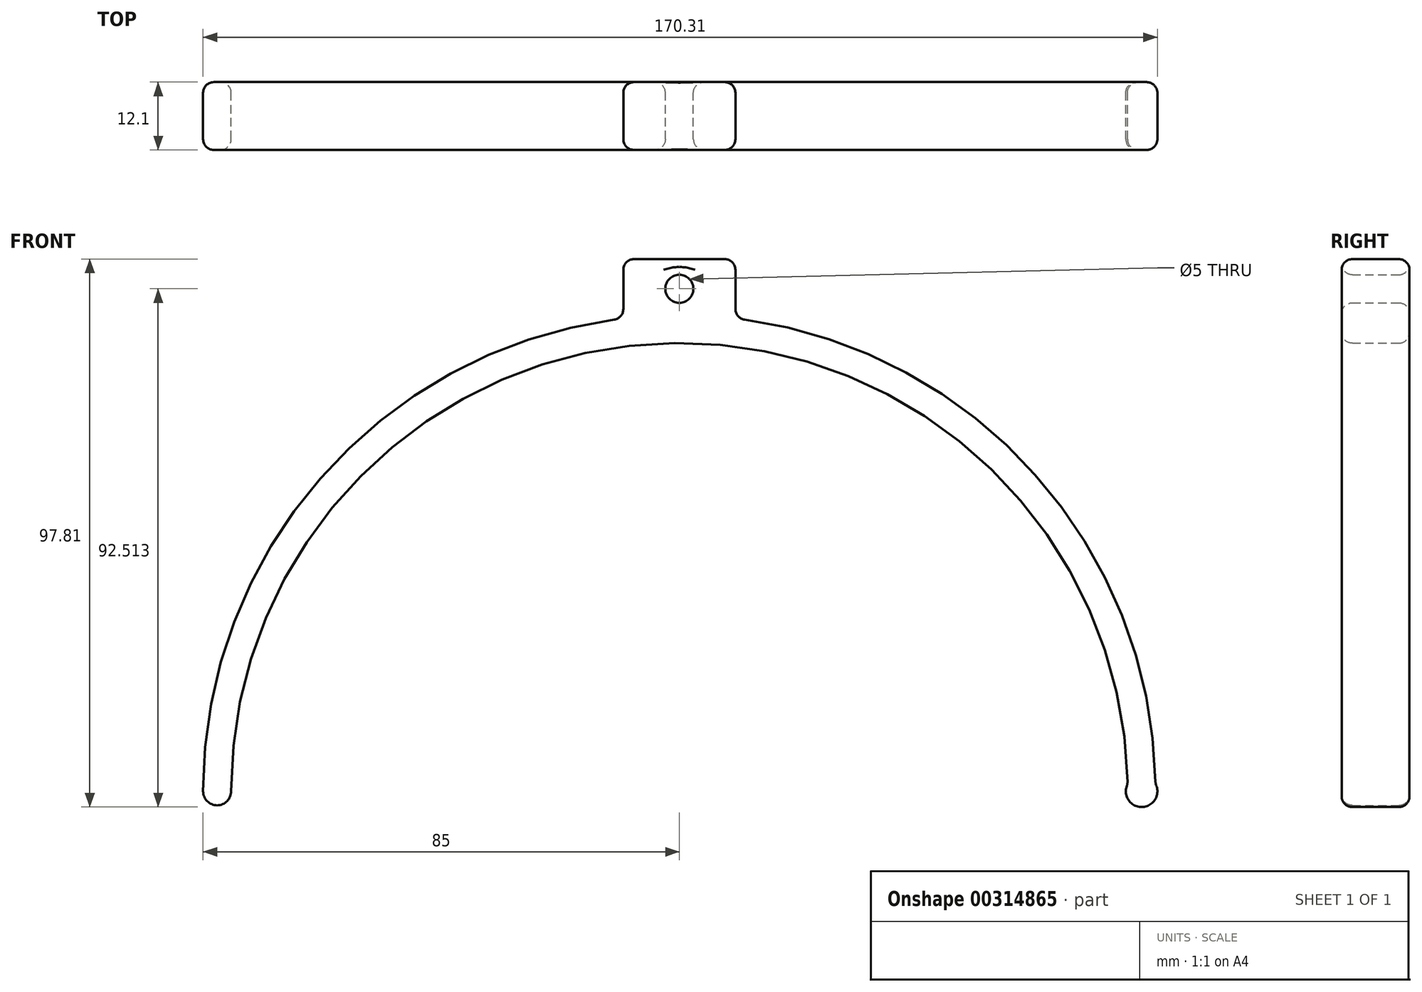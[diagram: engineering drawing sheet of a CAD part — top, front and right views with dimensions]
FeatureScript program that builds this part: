
annotation { "Feature Type Name" : "Feature", "Feature Type Description" : "" }
export const myFeature = defineFeature(function(context is Context, id is Id, definition is map)
    precondition{}
    {
        {
            var Q0;
            Q0=qCreatedBy(makeId("Front.planeOp"),FACE);
            var sketch = newSketch(context, id + "F0", { "sketchPlane" : qUnion([Q0])});
            skArc(sketch, "E0", {"start": v(79.99, -1.27) * mm, "mid": v(0.63, 80) * mm, "end": v(-80, 0) * mm});
            skArc(sketch, "E1", {"start": v(84.99, -1.3) * mm, "mid": v(63.97, 55.97) * mm, "end": v(10, 84.4) * mm});
            skLineSegment(sketch, "E2", {"start": v(0, 0) * mm, "end": v(0, 85) * mm, "construction": true});
            skLineSegment(sketch, "E3", {"start": v(0, 95) * mm, "end": v(10, 95) * mm, "construction": true});
            skLineSegment(sketch, "E4", {"start": v(0, 95) * mm, "end": v(-10, 95) * mm, "construction": true});
            skLineSegment(sketch, "E5", {"start": v(-10, 95) * mm, "end": v(-10, 84.4) * mm});
            skLineSegment(sketch, "E6", {"start": v(10, 95) * mm, "end": v(10, 84.4) * mm});
            skLineSegment(sketch, "E7", {"start": v(80, 0) * mm, "end": v(85, 0) * mm, "construction": true});
            skLineSegment(sketch, "E8", {"start": v(-80, 0) * mm, "end": v(-82.5, 0) * mm, "construction": true});
            skArc(sketch, "E9", {"start": v(-85, 0) * mm, "mid": v(-82.5, -2.5) * mm, "end": v(-80, 0) * mm});
            skArc(sketch, "E10", {"start": v(79.99, 1.27) * mm, "mid": v(82.52, -2.81) * mm, "end": v(84.99, 1.3) * mm});
            skLineSegment(sketch, "E11", {"start": v(-10, 95) * mm, "end": v(10, 95) * mm});
            skArc(sketch, "E12.trimOffspring", {"start": v(-10, 84.4) * mm, "mid": v(-63.54, 56.46) * mm, "end": v(-85, 0) * mm});
            skLineSegment(sketch, "E13", {"start": v(-10, 95) * mm, "end": v(10, 84.4) * mm, "construction": true});
            skLineSegment(sketch, "E14", {"start": v(10, 95) * mm, "end": v(-10, 84.4) * mm, "construction": true});
            skLineSegment(sketch, "E15.0", {"start": v(-80, 6.35) * mm, "end": v(-85, 6.35) * mm, "construction": true});
            skLineSegment(sketch, "E16.0", {"start": v(-80, 6.35) * mm, "end": v(-85, 6.35) * mm});
            skCircle(sketch, "E17", {"center": v(0, 89.7) * mm, "radius": 2.5 * mm});
            skSolve(sketch);
        }
        {
            var Q0;
            {var subQ0=sQuery(id+"F0.wireOp",EDGE,"E10");var subQ1=sQuery(id+"F0.wireOp",EDGE,"E0");var subQ2=makeQuery(id+"F0.imprint","INTERSECT",VERTEX,{"disambiguationData":[OD(0.0)],"derivedFrom":[subQ1,subQ0]});Q0=makeQuery(id+"F0.imprint","IMPRINT",FACE,{"disambiguationData":[TD([[makeQuery(id+"F0.imprint","IMPRINT",EDGE,{"disambiguationData":[TD([[subQ2,-1.0]])],"derivedFrom":subQ1}),1.0]])]});}
            var Q1;
            {var subQ0=sQuery(id+"F0.wireOp",EDGE,"E10");var subQ1=sQuery(id+"F0.wireOp",EDGE,"E1");var subQ2=makeQuery(id+"F0.imprint","INTERSECT",VERTEX,{"disambiguationData":[OD(0.0)],"derivedFrom":[subQ1,subQ0]});Q1=makeQuery(id+"F0.imprint","IMPRINT",FACE,{"disambiguationData":[TD([[makeQuery(id+"F0.imprint","IMPRINT",EDGE,{"disambiguationData":[TD([[subQ2,-1.0]])],"derivedFrom":subQ1}),-1.0]])]});}
            var Q2;
            {var subQ7=sQuery(id+"F0.wireOp",EDGE,"E5");Q2=makeQuery(id+"F0.imprint","IMPRINT",FACE,{"disambiguationData":[TD([[makeQuery(id+"F0.imprint","IMPRINT",EDGE,{"derivedFrom":subQ7}),1.0]])]});}
            extrude(context, id + "F1", {"entities" : qUnion([Q0, Q1, Q2]), "depth" : 12.1 * mm});
        }
        {
            var Q0;
            Q0=makeQuery(id+"F1.opExtrude","SWEPT_FACE",FACE,{"disambiguationData":[OSD([sQuery(id+"F0.wireOp",EDGE,"E11")])]});
            var Q1;
            Q1=makeQuery(id+"F1.opExtrude","CAP_EDGE",EDGE,{"disambiguationData":[OSD([sQuery(id+"F0.wireOp",EDGE,"E11")])],"isStart":false});
            var Q2;
            Q2=makeQuery(id+"F1.opExtrude","SWEPT_EDGE",EDGE,{"disambiguationData":[OSD([sQuery(id+"F0.wireOp",EDGE,"E6"),sQuery(id+"F0.wireOp",EDGE,"E11")])]});
            var Q3;
            Q3=makeQuery(id+"F1.opExtrude","SWEPT_EDGE",EDGE,{"disambiguationData":[OSD([sQuery(id+"F0.wireOp",EDGE,"E5"),sQuery(id+"F0.wireOp",EDGE,"E11")])]});
            var Q4;
            Q4=makeQuery(id+"F1.opExtrude","CAP_EDGE",EDGE,{"disambiguationData":[OSD([sQuery(id+"F0.wireOp",EDGE,"E11")])],"isStart":true});
            var Q5;
            Q5=makeQuery(id+"F1.opExtrude","CAP_EDGE",EDGE,{"disambiguationData":[OSD([sQuery(id+"F0.wireOp",EDGE,"E12.trimOffspring")])],"isStart":false});
            var Q6;
            Q6=makeQuery(id+"F1.opExtrude","CAP_EDGE",EDGE,{"disambiguationData":[OSD([sQuery(id+"F0.wireOp",EDGE,"E17")])],"isStart":false});
            var Q7;
            Q7=makeQuery(id+"F1.opExtrude","SWEPT_FACE",FACE,{"disambiguationData":[OSD([sQuery(id+"F0.wireOp",EDGE,"E6")])]});
            var Q8;
            Q8=makeQuery(id+"F1.opExtrude","SWEPT_FACE",FACE,{"disambiguationData":[OSD([sQuery(id+"F0.wireOp",EDGE,"E10")])]});
            var Q9;
            Q9=makeQuery(id+"F1.opExtrude","SWEPT_FACE",FACE,{"disambiguationData":[OSD([sQuery(id+"F0.wireOp",EDGE,"E17")])]});
            var Q10;
            Q10=makeQuery(id+"F1.opExtrude","CAP_EDGE",EDGE,{"disambiguationData":[OSD([sQuery(id+"F0.wireOp",EDGE,"E10")])],"isStart":false});
            var Q11;
            Q11=makeQuery(id+"F1.opExtrude","CAP_EDGE",EDGE,{"disambiguationData":[OSD([sQuery(id+"F0.wireOp",EDGE,"E1")])],"isStart":false});
            var Q12;
            Q12=makeQuery(id+"F1.opExtrude","CAP_EDGE",EDGE,{"disambiguationData":[OSD([sQuery(id+"F0.wireOp",EDGE,"E0")])],"isStart":false});
            var Q13;
            Q13=makeQuery(id+"F1.opExtrude","SWEPT_FACE",FACE,{"disambiguationData":[OSD([sQuery(id+"F0.wireOp",EDGE,"E12.trimOffspring")])]});
            var Q14;
            Q14=makeQuery(id+"F1.opExtrude","SWEPT_FACE",FACE,{"disambiguationData":[OSD([sQuery(id+"F0.wireOp",EDGE,"E9")])]});
            var Q15;
            Q15=makeQuery(id+"F1.opExtrude","SWEPT_FACE",FACE,{"disambiguationData":[OSD([sQuery(id+"F0.wireOp",EDGE,"E5")])]});
            var Q16;
            Q16=makeQuery(id+"F1.opExtrude","SWEPT_FACE",FACE,{"disambiguationData":[OSD([sQuery(id+"F0.wireOp",EDGE,"E1")])]});
            var Q17;
            Q17=makeQuery(id+"F1.opExtrude","CAP_FACE",FACE,{"disambiguationData":[OSD([sQuery(id+"F0.wireOp",EDGE,"E0"),sQuery(id+"F0.wireOp",EDGE,"E1"),sQuery(id+"F0.wireOp",EDGE,"E5"),sQuery(id+"F0.wireOp",EDGE,"E6"),sQuery(id+"F0.wireOp",EDGE,"E9"),sQuery(id+"F0.wireOp",EDGE,"E10"),sQuery(id+"F0.wireOp",EDGE,"E11"),sQuery(id+"F0.wireOp",EDGE,"E12.trimOffspring"),sQuery(id+"F0.wireOp",EDGE,"E17")])],"isStart":false});
            var Q18;
            Q18=makeQuery(id+"F1.opExtrude","CAP_EDGE",EDGE,{"disambiguationData":[OSD([sQuery(id+"F0.wireOp",EDGE,"E9")])],"isStart":false});
            var Q19;
            Q19=makeQuery(id+"F1.opExtrude","CAP_EDGE",EDGE,{"disambiguationData":[OSD([sQuery(id+"F0.wireOp",EDGE,"E17")])],"isStart":true});
            var Q20;
            Q20=makeQuery(id+"F1.opExtrude","CAP_EDGE",EDGE,{"disambiguationData":[OSD([sQuery(id+"F0.wireOp",EDGE,"E12.trimOffspring")])],"isStart":true});
            var Q21;
            Q21=makeQuery(id+"F1.opExtrude","CAP_EDGE",EDGE,{"disambiguationData":[OSD([sQuery(id+"F0.wireOp",EDGE,"E10")])],"isStart":true});
            var Q22;
            Q22=makeQuery(id+"F1.opExtrude","CAP_EDGE",EDGE,{"disambiguationData":[OSD([sQuery(id+"F0.wireOp",EDGE,"E1")])],"isStart":true});
            var Q23;
            Q23=makeQuery(id+"F1.opExtrude","CAP_EDGE",EDGE,{"disambiguationData":[OSD([sQuery(id+"F0.wireOp",EDGE,"E0")])],"isStart":true});
            var Q24;
            Q24=makeQuery(id+"F1.opExtrude","SWEPT_EDGE",EDGE,{"disambiguationData":[OSD([sQuery(id+"F0.wireOp",EDGE,"E1"),sQuery(id+"F0.wireOp",EDGE,"E10")])]});
            var Q25;
            Q25=makeQuery(id+"F1.opExtrude","SWEPT_EDGE",EDGE,{"disambiguationData":[OSD([sQuery(id+"F0.wireOp",EDGE,"E0"),sQuery(id+"F0.wireOp",EDGE,"E10")])]});
            var Q26;
            Q26=makeQuery(id+"F1.opExtrude","CAP_FACE",FACE,{"disambiguationData":[OSD([sQuery(id+"F0.wireOp",EDGE,"E0"),sQuery(id+"F0.wireOp",EDGE,"E1"),sQuery(id+"F0.wireOp",EDGE,"E5"),sQuery(id+"F0.wireOp",EDGE,"E6"),sQuery(id+"F0.wireOp",EDGE,"E9"),sQuery(id+"F0.wireOp",EDGE,"E10"),sQuery(id+"F0.wireOp",EDGE,"E11"),sQuery(id+"F0.wireOp",EDGE,"E12.trimOffspring"),sQuery(id+"F0.wireOp",EDGE,"E17")])],"isStart":true});
            var Q27;
            Q27=makeQuery(id+"F1.opExtrude","SWEPT_FACE",FACE,{"disambiguationData":[OSD([sQuery(id+"F0.wireOp",EDGE,"E0")])]});
            var Q28;
            Q28=makeQuery(id+"F1.opExtrude","CAP_EDGE",EDGE,{"disambiguationData":[OSD([sQuery(id+"F0.wireOp",EDGE,"E6")])],"isStart":false});
            var Q29;
            Q29=makeQuery(id+"F1.opExtrude","CAP_EDGE",EDGE,{"disambiguationData":[OSD([sQuery(id+"F0.wireOp",EDGE,"E5")])],"isStart":false});
            var Q30;
            Q30=makeQuery(id+"F1.opExtrude","CAP_EDGE",EDGE,{"disambiguationData":[OSD([sQuery(id+"F0.wireOp",EDGE,"E9")])],"isStart":true});
            var Q31;
            Q31=makeQuery(id+"F1.opExtrude","CAP_EDGE",EDGE,{"disambiguationData":[OSD([sQuery(id+"F0.wireOp",EDGE,"E5")])],"isStart":true});
            var Q32;
            Q32=makeQuery(id+"F1.opExtrude","SWEPT_EDGE",EDGE,{"disambiguationData":[OSD([sQuery(id+"F0.wireOp",EDGE,"E9"),sQuery(id+"F0.wireOp",EDGE,"E12.trimOffspring")])]});
            var Q33;
            Q33=makeQuery(id+"F1.opExtrude","SWEPT_EDGE",EDGE,{"disambiguationData":[OSD([sQuery(id+"F0.wireOp",EDGE,"E5"),sQuery(id+"F0.wireOp",EDGE,"E12.trimOffspring")])]});
            var Q34;
            Q34=makeQuery(id+"F1.opExtrude","SWEPT_EDGE",EDGE,{"disambiguationData":[OSD([sQuery(id+"F0.wireOp",EDGE,"E1"),sQuery(id+"F0.wireOp",EDGE,"E6")])]});
            var Q35;
            Q35=makeQuery(id+"F1.opExtrude","SWEPT_EDGE",EDGE,{"disambiguationData":[OSD([sQuery(id+"F0.wireOp",EDGE,"E0"),sQuery(id+"F0.wireOp",EDGE,"E9")])]});
            var Q36;
            Q36=makeQuery(id+"F1.opExtrude","CAP_EDGE",EDGE,{"disambiguationData":[OSD([sQuery(id+"F0.wireOp",EDGE,"E6")])],"isStart":true});
            fillet(context, id + "F2", {"entities" : qUnion([Q0, Q1, Q2, Q3, Q4, Q5, Q6, Q7, Q8, Q9, Q10, Q11, Q12, Q13, Q14, Q15, Q16, Q17, Q18, Q19, Q20, Q21, Q22, Q23, Q24, Q25, Q26, Q27, Q28, Q29, Q30, Q31, Q32, Q33, Q34, Q35, Q36]), "radius" : 1.9 * mm, "tangentPropagation" : true, "allowEdgeOverflow" : false});
        }
    });
